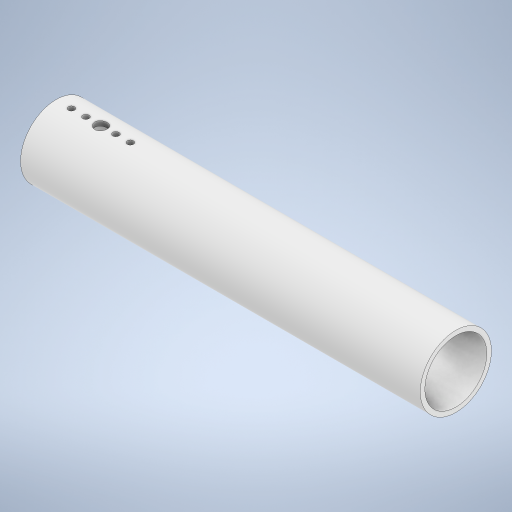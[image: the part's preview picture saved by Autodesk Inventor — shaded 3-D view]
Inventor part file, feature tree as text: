
AUTODESK INVENTOR PART (.ipt)
format: ipt  version: 2023 (Build 270158030, 158C)  size: 275,968 bytes
history: native  units: in
note: dims shown in document units (in); Inventor stores cm internally (conversion verified against a paired STEP export)
features: extrude x3, sketch x3
ambient origin geometry x8: Origin, YZ Plane, XZ Plane, XY Plane, X Axis, Y Axis, Z Axis, Center Point
bodies: Solid1 (feature_tree)
feature tree (6):
  extrude  "Extrusion1"  Depth=0.154in
  extrude  "Extrusion2"  Depth=0.4134in
  extrude  "Extrusion3"  TaperAngle=0.0deg  [1 undecoded]
  sketch  "Sketch1"  dims[d0=2.067in d1=0.154in]
  sketch  "Sketch2"  dims[d2=13.3465in d3=0.0in d4=0.4134in]
  sketch  "Sketch3"  dims[d5=1.5in d6=0.0in d7=0.0in d8=0.2067in d9=1.9685in d10=1.4961in d11=0.0in d12=0.0in d13=0.2067in d14=1.0in]
note: 1 required parameter value undecoded (feature->parameter linkage not recoverable at this tier; creation-order binding heuristic only, values carry confidence <= 0.55)
